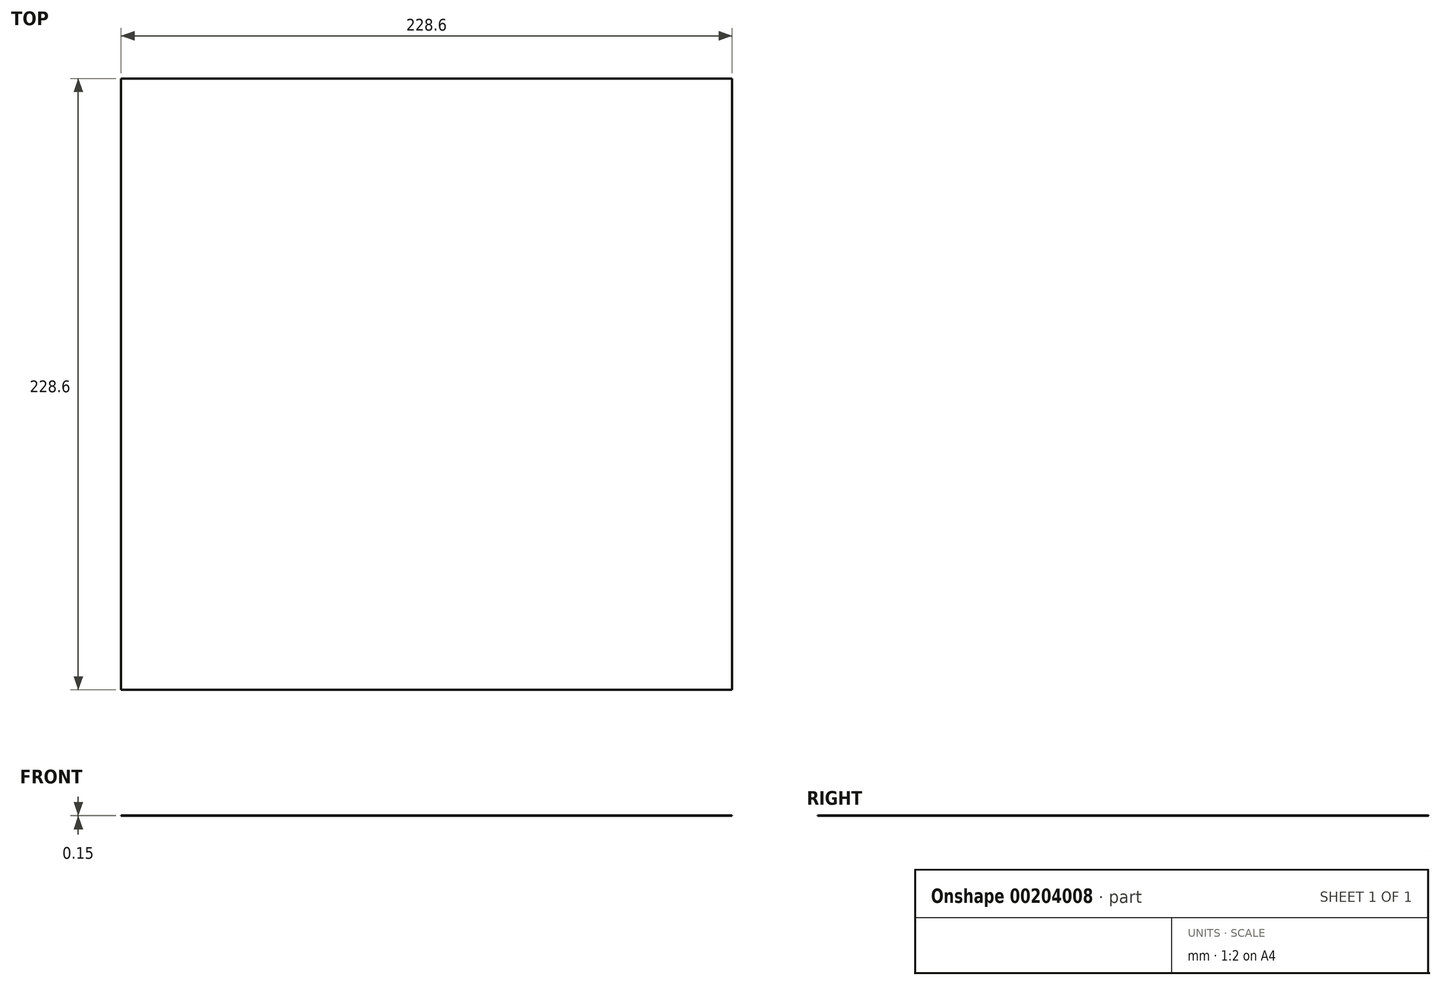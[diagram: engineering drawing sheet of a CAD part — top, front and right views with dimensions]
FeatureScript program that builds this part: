
annotation { "Feature Type Name" : "Feature", "Feature Type Description" : "" }
export const myFeature = defineFeature(function(context is Context, id is Id, definition is map)
    precondition{}
    {
        {
            var Q0;
            Q0=qCreatedBy(makeId("Top.planeOp"),FACE);
            var sketch = newSketch(context, id + "F0", { "sketchPlane" : qUnion([Q0])});
            skLineSegment(sketch, "E0.bottom", {"start": v(117.65, -114.3) * mm, "end": v(-110.95, -114.3) * mm});
            skLineSegment(sketch, "E0.top", {"start": v(117.65, 114.3) * mm, "end": v(-110.95, 114.3) * mm});
            skLineSegment(sketch, "E0.left", {"start": v(117.65, -114.3) * mm, "end": v(117.65, 114.3) * mm});
            skLineSegment(sketch, "E0.right", {"start": v(-110.95, -114.3) * mm, "end": v(-110.95, 114.3) * mm});
            skPoint(sketch, "E0.middle", {"position": v(3.35, 0) * mm});
            skSolve(sketch);
        }
        {
            var Q0;
            Q0 = qSketchRegion(id + "F0", true);
            extrude(context, id + "F1", {"entities" : qUnion([Q0]), "depth" : 0.15 * mm});
        }
    });
